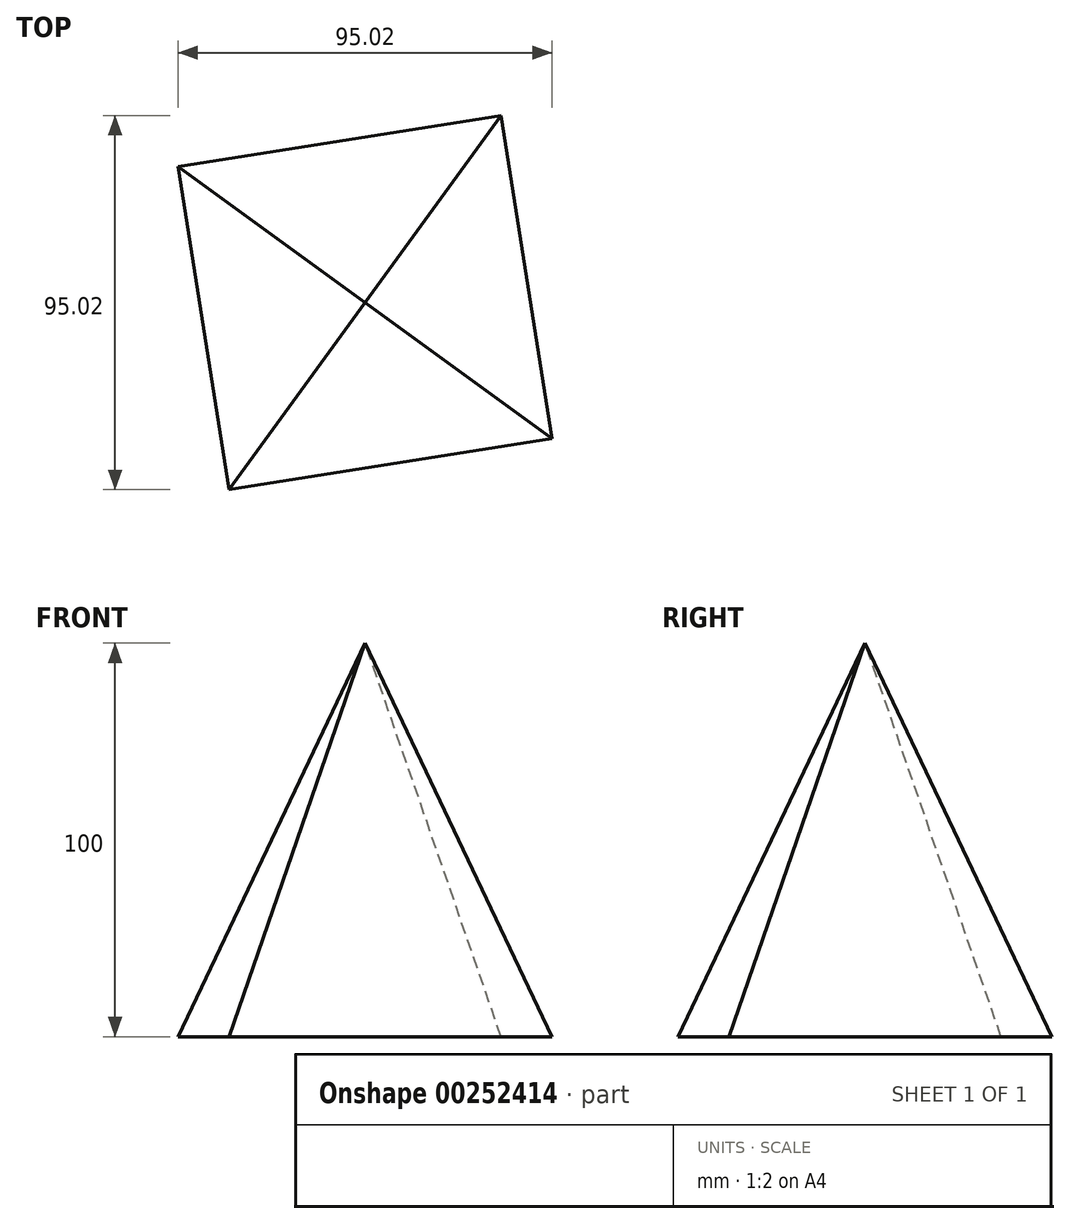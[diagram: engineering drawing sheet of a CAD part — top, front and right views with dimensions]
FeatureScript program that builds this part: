
annotation { "Feature Type Name" : "Feature", "Feature Type Description" : "" }
export const myFeature = defineFeature(function(context is Context, id is Id, definition is map)
    precondition{}
    {
        {
            var Q0;
            Q0=qCreatedBy(makeId("Top.planeOp"),FACE);
            var sketch = newSketch(context, id + "F0", { "sketchPlane" : qUnion([Q0])});
            skCircle(sketch, "E0.cCircle", {"center": v(0, 0) * mm, "radius": 58.74 * mm, "construction": true});
            skLineSegment(sketch, "E0.0", {"start": v(-47.51, 34.54) * mm, "end": v(34.54, 47.51) * mm});
            skLineSegment(sketch, "E0.1", {"start": v(34.54, 47.51) * mm, "end": v(47.51, -34.54) * mm});
            skLineSegment(sketch, "E0.2", {"start": v(47.51, -34.54) * mm, "end": v(-34.54, -47.51) * mm});
            skLineSegment(sketch, "E0.3", {"start": v(-34.54, -47.51) * mm, "end": v(-47.51, 34.54) * mm});
            skSolve(sketch);
        }
        {
            var Q0;
            Q0=qCreatedBy(makeId("Top.planeOp"),FACE);
            cPlane(context, id + "F1", {"entities" : qUnion([Q0]), "cplaneType" : CPlaneType.OFFSET, "offset" : 100 * mm, "width" : 152.4 * mm, "height" : 152.4 * mm});
        }
        {
            var Q0;
            Q0=qCreatedBy(id+"F1.planeOp",FACE);
            var sketch = newSketch(context, id + "F2", { "sketchPlane" : qUnion([Q0])});
            skPoint(sketch, "E1", {"position": v(0, 0) * mm});
            skSolve(sketch);
        }
        {
            var Q0;
            Q0=makeQuery(id+"F0.imprint","IMPRINT",FACE,{"disambiguationData":[TD([[makeQuery(id+"F0.imprint","IMPRINT",EDGE,{"derivedFrom":sQuery(id+"F0.wireOp",EDGE,"E0.0")}),-1.0]])]});
            var Q1;
            Q1=sQuery(id+"F2.wireOp",VERTEX,"E1");
            loft(context, id + "F3", {"sheetProfilesArray" : [{ "sheetProfileEntities" : qUnion([Q0]) }, { "sheetProfileEntities" : qUnion([Q1]) }]});
        }
    });
